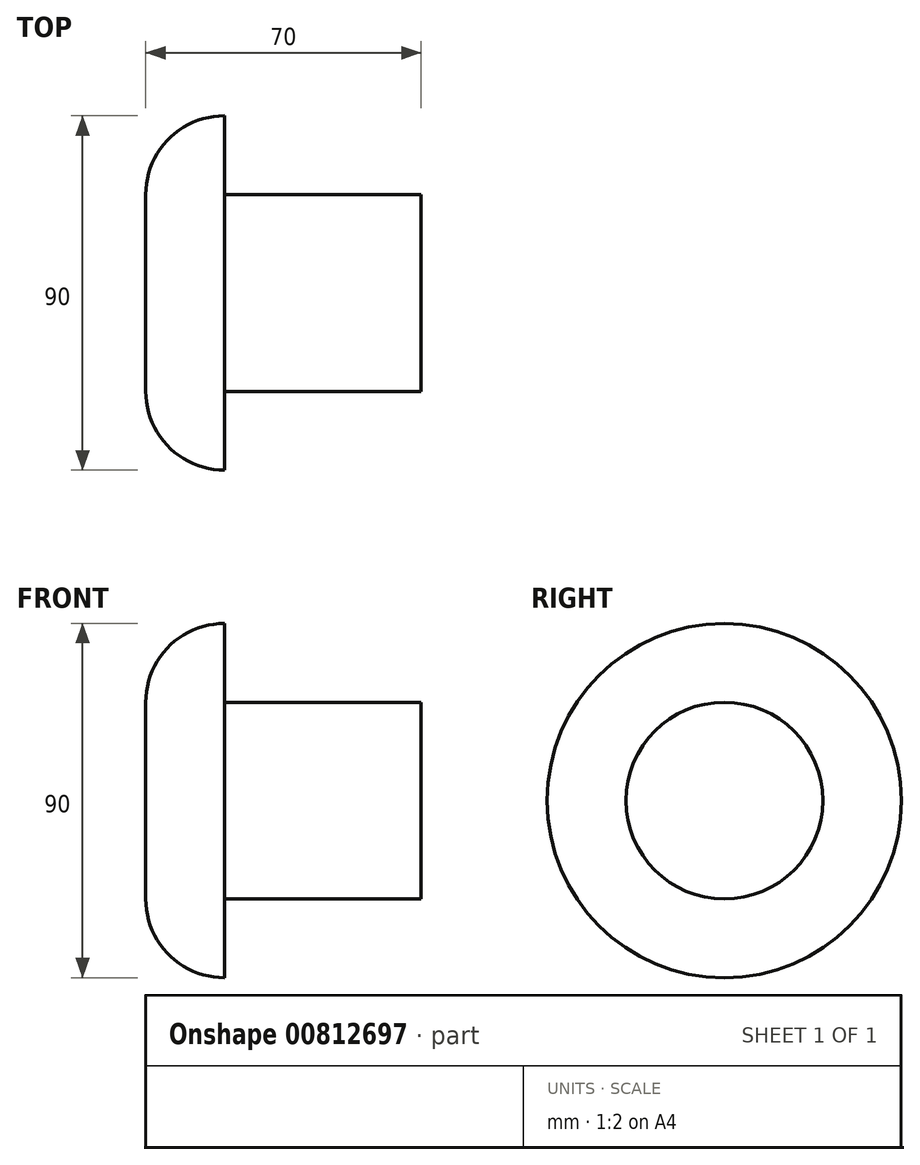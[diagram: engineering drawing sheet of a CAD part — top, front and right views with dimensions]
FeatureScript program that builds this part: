
annotation { "Feature Type Name" : "Feature", "Feature Type Description" : "" }
export const myFeature = defineFeature(function(context is Context, id is Id, definition is map)
    precondition{}
    {
        {
            var Q0;
            Q0=qCreatedBy(makeId("Right.planeOp"),FACE);
            var sketch = newSketch(context, id + "F0", { "sketchPlane" : qUnion([Q0])});
            skCircle(sketch, "E0", {"center": v(0, 0) * mm, "radius": 25 * mm});
            skCircle(sketch, "E1", {"center": v(0, 0) * mm, "radius": 45 * mm});
            skSolve(sketch);
        }
        {
            var Q0;
            Q0=makeQuery(id+"F0.imprint","IMPRINT",FACE,{"disambiguationData":[TD([[makeQuery(id+"F0.imprint","IMPRINT",EDGE,{"derivedFrom":sQuery(id+"F0.wireOp",EDGE,"E0")}),1.0]])]});
            extrude(context, id + "F1", {"entities" : qUnion([Q0]), "depth" : 50 * mm, "offsetDistance" : 25 * mm});
        }
        {
            var Q0;
            Q0=makeQuery(id+"F0.imprint","IMPRINT",FACE,{"disambiguationData":[TD([[makeQuery(id+"F0.imprint","IMPRINT",EDGE,{"derivedFrom":sQuery(id+"F0.wireOp",EDGE,"E0")}),-1.0]])]});
            var Q1;
            Q1=makeQuery(id+"F0.imprint","IMPRINT",FACE,{"disambiguationData":[TD([[makeQuery(id+"F0.imprint","IMPRINT",EDGE,{"derivedFrom":sQuery(id+"F0.wireOp",EDGE,"E0")}),1.0]])]});
            extrude(context, id + "F2", {"entities" : qUnion([Q0, Q1]), "oppositeDirection" : true, "depth" : 20 * mm, "offsetDistance" : 25 * mm});
        }
        {
            var Q0;
            Q0=makeQuery(id+"F2.opExtrude","CAP_FACE",FACE,{"disambiguationData":[OSD([sQuery(id+"F0.wireOp",EDGE,"E1")])],"isStart":false});
            fillet(context, id + "F3", {"entities" : qUnion([Q0]), "radius" : 20 * mm, "tangentPropagation" : true, "allowEdgeOverflow" : false});
        }
    });
